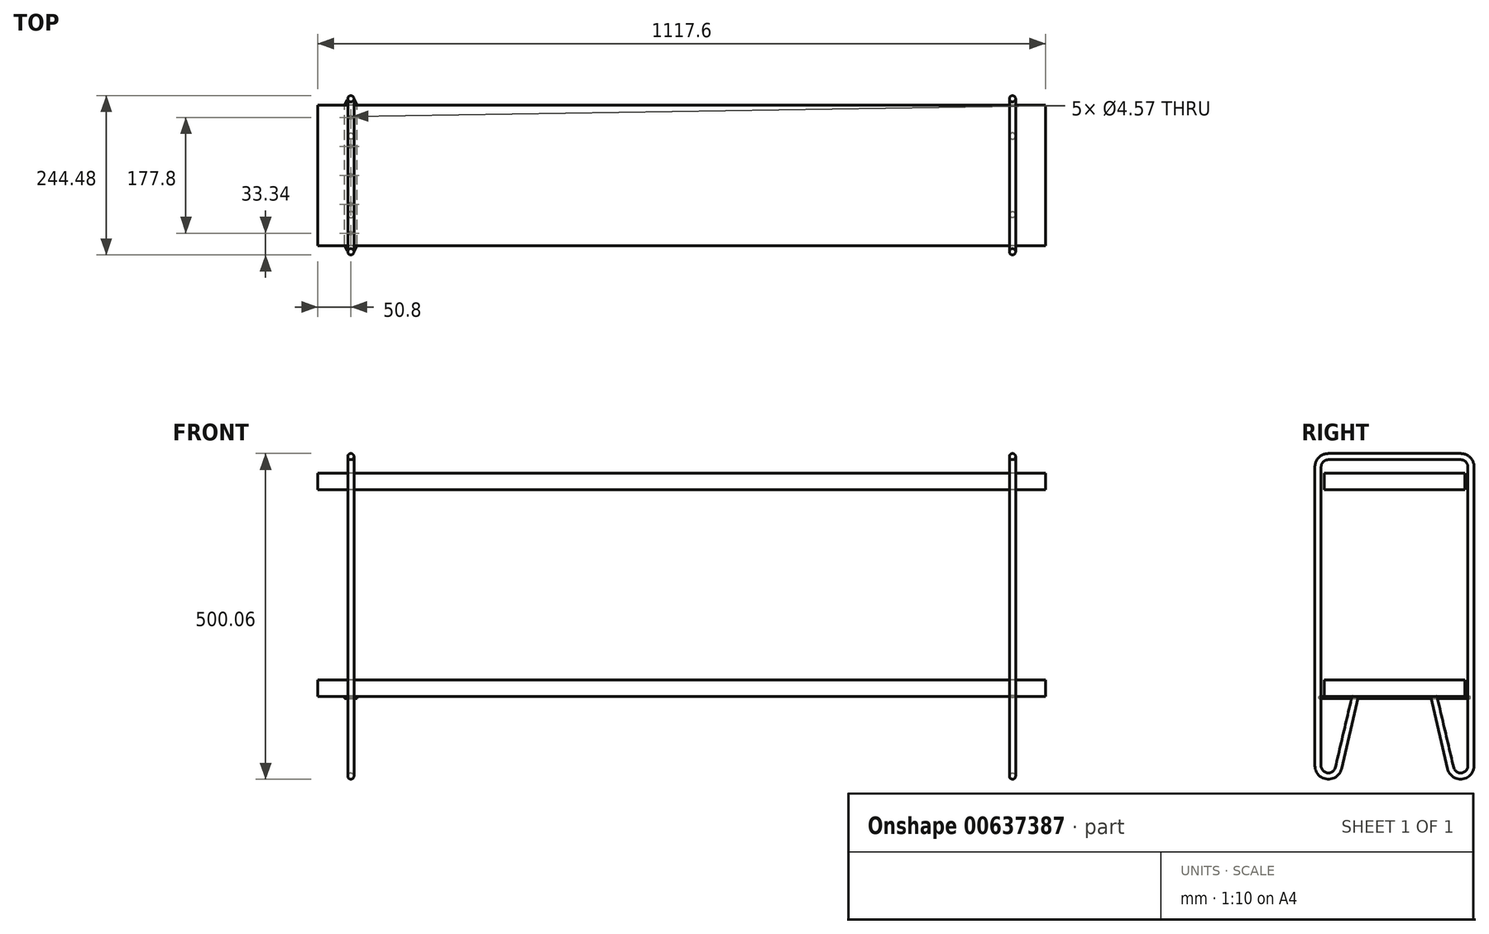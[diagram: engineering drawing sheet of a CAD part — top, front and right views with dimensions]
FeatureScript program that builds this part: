
annotation { "Feature Type Name" : "Feature", "Feature Type Description" : "" }
export const myFeature = defineFeature(function(context is Context, id is Id, definition is map)
    precondition{}
    {
        {
            var Q0;
            Q0=qCreatedBy(makeId("Right.planeOp"),FACE);
            var sketch = newSketch(context, id + "F0", { "sketchPlane" : qUnion([Q0])});
            skLineSegment(sketch, "E0", {"start": v(0, 0) * mm, "end": v(-101.6, 0) * mm});
            skLineSegment(sketch, "E1", {"start": v(-117.47, -15.88) * mm, "end": v(-117.47, -474.66) * mm});
            skLineSegment(sketch, "E2", {"start": v(-86.15, -478.3) * mm, "end": v(-60.32, -368.3) * mm});
            skLineSegment(sketch, "E3.bottom", {"start": v(-107.95, -342.9) * mm, "end": v(107.95, -342.9) * mm, "construction": true});
            skLineSegment(sketch, "E3.top", {"start": v(-107.95, -368.3) * mm, "end": v(107.95, -368.3) * mm, "construction": true});
            skLineSegment(sketch, "E3.left", {"start": v(-107.95, -342.9) * mm, "end": v(-107.95, -368.3) * mm, "construction": true});
            skLineSegment(sketch, "E3.right", {"start": v(107.95, -342.9) * mm, "end": v(107.95, -368.3) * mm, "construction": true});
            skLineSegment(sketch, "E4.bottom", {"start": v(-107.95, -25.4) * mm, "end": v(107.95, -25.4) * mm, "construction": true});
            skLineSegment(sketch, "E4.top", {"start": v(-107.95, -50.8) * mm, "end": v(107.95, -50.8) * mm, "construction": true});
            skLineSegment(sketch, "E4.left", {"start": v(-107.95, -25.4) * mm, "end": v(-107.95, -50.8) * mm, "construction": true});
            skLineSegment(sketch, "E4.right", {"start": v(107.95, -25.4) * mm, "end": v(107.95, -50.8) * mm, "construction": true});
            skLineSegment(sketch, "E5", {"start": v(-668.57, -495.3) * mm, "end": v(1361.26, -495.3) * mm, "construction": true});
            skArc(sketch, "E6", {"start": v(-117.48, -474.66) * mm, "mid": v(-103.43, -490.43) * mm, "end": v(-86.15, -478.3) * mm});
            skArc(sketch, "E7", {"start": v(-101.6, 0) * mm, "mid": v(-112.83, -4.65) * mm, "end": v(-117.47, -15.88) * mm});
            skLineSegment(sketch, "E8", {"start": v(0, -25.4) * mm, "end": v(0, 117.18) * mm, "construction": true});
            skLineSegment(sketch, "E9.MirrorCS", {"start": v(0, 0) * mm, "end": v(101.6, 0) * mm});
            skArc(sketch, "E10.MirrorCS", {"start": v(101.6, 0) * mm, "mid": v(112.83, -4.65) * mm, "end": v(117.48, -15.88) * mm});
            skLineSegment(sketch, "E11.MirrorCS", {"start": v(117.48, -15.88) * mm, "end": v(117.48, -474.66) * mm});
            skArc(sketch, "E12.MirrorCS", {"start": v(117.48, -474.66) * mm, "mid": v(103.43, -490.43) * mm, "end": v(86.15, -478.3) * mm});
            skLineSegment(sketch, "E13.MirrorCS", {"start": v(86.15, -478.3) * mm, "end": v(60.33, -368.3) * mm});
            skLineSegment(sketch, "E14.0", {"start": v(-90.78, -477.2) * mm, "end": v(-63.93, -362.81) * mm, "construction": true});
            skArc(sketch, "E14.1", {"start": v(-112.71, -474.66) * mm, "mid": v(-102.88, -485.7) * mm, "end": v(-90.78, -477.2) * mm, "construction": true});
            skLineSegment(sketch, "E14.2", {"start": v(-112.71, -15.88) * mm, "end": v(-112.71, -474.66) * mm, "construction": true});
            skArc(sketch, "E14.3", {"start": v(-101.6, -4.76) * mm, "mid": v(-109.46, -8.02) * mm, "end": v(-112.71, -15.88) * mm, "construction": true});
            skLineSegment(sketch, "E14.4", {"start": v(0, -4.76) * mm, "end": v(-101.6, -4.76) * mm, "construction": true});
            skLineSegment(sketch, "E14.5", {"start": v(0, -4.76) * mm, "end": v(101.6, -4.76) * mm, "construction": true});
            skLineSegment(sketch, "E14.6", {"start": v(90.78, -477.2) * mm, "end": v(64.62, -365.77) * mm, "construction": true});
            skArc(sketch, "E14.7", {"start": v(112.71, -474.66) * mm, "mid": v(102.88, -485.7) * mm, "end": v(90.78, -477.2) * mm, "construction": true});
            skLineSegment(sketch, "E14.8", {"start": v(112.71, -15.88) * mm, "end": v(112.71, -474.66) * mm, "construction": true});
            skArc(sketch, "E14.9", {"start": v(101.6, -4.76) * mm, "mid": v(109.46, -8.02) * mm, "end": v(112.71, -15.88) * mm, "construction": true});
            skLineSegment(sketch, "E15.0", {"start": v(-81.5, -479.38) * mm, "end": v(-55.62, -369.1) * mm, "construction": true});
            skArc(sketch, "E15.1", {"start": v(-122.24, -474.66) * mm, "mid": v(-103.97, -495.16) * mm, "end": v(-81.5, -479.38) * mm, "construction": true});
            skLineSegment(sketch, "E15.2", {"start": v(-122.24, -15.88) * mm, "end": v(-122.24, -474.66) * mm, "construction": true});
            skArc(sketch, "E15.3", {"start": v(-101.6, 4.76) * mm, "mid": v(-116.2, -1.28) * mm, "end": v(-122.24, -15.88) * mm, "construction": true});
            skLineSegment(sketch, "E15.4", {"start": v(0, 4.76) * mm, "end": v(-101.6, 4.76) * mm, "construction": true});
            skLineSegment(sketch, "E15.5", {"start": v(0, 4.76) * mm, "end": v(101.6, 4.76) * mm, "construction": true});
            skLineSegment(sketch, "E15.6", {"start": v(81.5, -479.38) * mm, "end": v(55.7, -369.44) * mm, "construction": true});
            skArc(sketch, "E15.7", {"start": v(122.24, -474.66) * mm, "mid": v(103.97, -495.16) * mm, "end": v(81.5, -479.38) * mm, "construction": true});
            skLineSegment(sketch, "E15.8", {"start": v(122.24, -15.88) * mm, "end": v(122.24, -474.66) * mm, "construction": true});
            skArc(sketch, "E15.9", {"start": v(101.6, 4.76) * mm, "mid": v(116.2, -1.28) * mm, "end": v(122.24, -15.88) * mm, "construction": true});
            skSolve(sketch);
        }
        {
            var Q0;
            Q0=qCreatedBy(makeId("Front.planeOp"),FACE);
            var sketch = newSketch(context, id + "F1", { "sketchPlane" : qUnion([Q0])});
            skCircle(sketch, "E16", {"center": v(0, 0) * mm, "radius": 4.76 * mm});
            skSolve(sketch);
        }
        {
            var Q0;
            Q0 = qSketchRegion(id + "F1", true);
            var Q1;
            Q1 = qConstructionFilter(qBodyType(qCreatedBy(id + "F0" ,EDGE), BodyType.WIRE), ConstructionObject.NO);
            sweep(context, id + "F2", {"profiles" : qUnion([Q0]), "path" : qUnion([Q1])});
        }
        {
            var Q0;
            Q0=qCreatedBy(makeId("Right.planeOp"),FACE);
            cPlane(context, id + "F3", {"entities" : qUnion([Q0]), "cplaneType" : CPlaneType.OFFSET, "offset" : 508 * mm, "width" : 152.4 * mm, "height" : 152.4 * mm});
        }
        {
            var Q0;
            Q0=makeQuery(id+"F2.opSweep","SWEPT_BODY",BODY,{"disambiguationData":[OSD([sQuery(id+"F0.wireOp",EDGE,"E13.MirrorCS"),sQuery(id+"F1.wireOp",EDGE,"E16")])]});
            var Q1;
            Q1=qCreatedBy(id+"F3.planeOp",FACE);
            mirror(context, id + "F4", {"entities" : qUnion([Q0]), "mirrorPlane" : qUnion([Q1])});
        }
        {
            var Q0;
            Q0=qCreatedBy(id+"F3.planeOp",FACE);
            var sketch = newSketch(context, id + "F5", { "sketchPlane" : qUnion([Q0])});
            skLineSegment(sketch, "E17.0", {"start": v(-107.95, -25.4) * mm, "end": v(107.95, -25.4) * mm});
            skLineSegment(sketch, "E18.0", {"start": v(-107.95, -50.8) * mm, "end": v(107.95, -50.8) * mm});
            skLineSegment(sketch, "E19.0", {"start": v(107.95, -25.4) * mm, "end": v(107.95, -50.8) * mm});
            skLineSegment(sketch, "E20.0", {"start": v(-107.95, -25.4) * mm, "end": v(-107.95, -50.8) * mm});
            skLineSegment(sketch, "E21.0", {"start": v(-107.95, -342.9) * mm, "end": v(-107.95, -368.3) * mm});
            skLineSegment(sketch, "E22.0", {"start": v(-107.95, -368.3) * mm, "end": v(107.95, -368.3) * mm});
            skLineSegment(sketch, "E23.0", {"start": v(-107.95, -342.9) * mm, "end": v(107.95, -342.9) * mm});
            skLineSegment(sketch, "E24.0", {"start": v(107.95, -342.9) * mm, "end": v(107.95, -368.3) * mm});
            skSolve(sketch);
        }
        {
            var Q0;
            Q0 = qSketchRegion(id + "F5", true);
            var Q1;
            Q1 = qConstructionFilter(qBodyType(qCreatedBy(id + "F5" ,EDGE), BodyType.WIRE), ConstructionObject.NO);
            extrude(context, id + "F6", {"entities" : qUnion([Q0]), "surfaceEntities" : qUnion([Q1]), "depth" : 558.8 * mm, "offsetDistance" : 25.4 * mm, "hasSecondDirection" : true, "secondDirectionOppositeDirection" : true, "secondDirectionDepth" : 558.8 * mm});
        }
        {
            var Q0;
            Q0=makeQuery(id+"F6.opExtrude","SWEPT_FACE",FACE,{"disambiguationData":[OSD([sQuery(id+"F5.wireOp",EDGE,"E22.0")])]});
            var sketch = newSketch(context, id + "F7", { "sketchPlane" : qUnion([Q0])});
            skArc(sketch, "E25.0", {"start": v(-4.76, 117.47) * mm, "mid": v(0, 112.71) * mm, "end": v(4.76, 117.47) * mm});
            skArc(sketch, "E26.0", {"start": v(4.76, -117.47) * mm, "mid": v(0, -112.71) * mm, "end": v(-4.76, -117.47) * mm});
            skLineSegment(sketch, "E27.left", {"start": v(-9.53, 107.95) * mm, "end": v(-9.53, -107.95) * mm});
            skLineSegment(sketch, "E27.right", {"start": v(9.52, 107.95) * mm, "end": v(9.53, -107.95) * mm});
            skLineSegment(sketch, "E28", {"start": v(-4.76, 117.47) * mm, "end": v(-9.53, 107.95) * mm});
            skLineSegment(sketch, "E29", {"start": v(4.76, 117.47) * mm, "end": v(9.52, 107.95) * mm});
            skLineSegment(sketch, "E30", {"start": v(-4.76, -117.47) * mm, "end": v(-9.53, -107.95) * mm});
            skLineSegment(sketch, "E31", {"start": v(9.53, -107.95) * mm, "end": v(4.76, -117.47) * mm});
            skPoint(sketch, "E32.orphan", {"position": v(9.53, -117.47) * mm});
            skPoint(sketch, "E33.orphan", {"position": v(-9.53, 117.47) * mm});
            skPoint(sketch, "E34.orphan", {"position": v(9.52, 117.47) * mm});
            skLineSegment(sketch, "E35", {"start": v(0, 117.47) * mm, "end": v(0, -117.47) * mm, "construction": true});
            skLineSegment(sketch, "E36", {"start": v(-9.53, 0) * mm, "end": v(9.52, 0) * mm, "construction": true});
            skCircle(sketch, "E37", {"center": v(0, 0) * mm, "radius": 2.29 * mm});
            skCircle(sketch, "E38", {"center": v(0, 44.45) * mm, "radius": 2.29 * mm});
            skCircle(sketch, "E39", {"center": v(0, 88.9) * mm, "radius": 2.29 * mm});
            skCircle(sketch, "E40.MirrorC", {"center": v(0, -44.45) * mm, "radius": 2.29 * mm});
            skCircle(sketch, "E41.MirrorC", {"center": v(0, -88.9) * mm, "radius": 2.29 * mm});
            skSolve(sketch);
        }
        {
            var Q0;
            Q0 = qSketchRegion(id + "F7", true);
            extrude(context, id + "F8", {"entities" : qUnion([Q0]), "depth" : 3.17 * mm, "offsetDistance" : 25.4 * mm});
        }
        {
            var Q0;
            Q0=makeQuery(id+"F8.opExtrude","SWEPT_EDGE",EDGE,{"disambiguationData":[OSD([sQuery(id+"F7.wireOp",EDGE,"E25.0"),sQuery(id+"F7.wireOp",EDGE,"E28")])]});
            var Q1;
            Q1=makeQuery(id+"F8.opExtrude","SWEPT_EDGE",EDGE,{"disambiguationData":[OSD([sQuery(id+"F7.wireOp",EDGE,"E25.0"),sQuery(id+"F7.wireOp",EDGE,"E29")])]});
            var Q2;
            Q2=makeQuery(id+"F8.opExtrude","SWEPT_EDGE",EDGE,{"disambiguationData":[OSD([sQuery(id+"F7.wireOp",EDGE,"E26.0"),sQuery(id+"F7.wireOp",EDGE,"E31")])]});
            var Q3;
            Q3=makeQuery(id+"F8.opExtrude","SWEPT_EDGE",EDGE,{"disambiguationData":[OSD([sQuery(id+"F7.wireOp",EDGE,"E26.0"),sQuery(id+"F7.wireOp",EDGE,"E30")])]});
            fillet(context, id + "F9", {"entities" : qUnion([Q0, Q1, Q2, Q3]), "radius" : 0.64 * mm, "tangentPropagation" : true, "allowEdgeOverflow" : false});
        }
        {
            var Q0;
            Q0=makeQuery(id+"F8.opExtrude","SWEPT_EDGE",EDGE,{"disambiguationData":[OSD([sQuery(id+"F5.wireOp",EDGE,"E22.0"),sQuery(id+"F5.wireOp",EDGE,"E24.0"),sQuery(id+"F7.wireOp",EDGE,"E27.left"),sQuery(id+"F7.wireOp",EDGE,"E30")])]});
            var Q1;
            Q1=makeQuery(id+"F8.opExtrude","SWEPT_EDGE",EDGE,{"disambiguationData":[OSD([sQuery(id+"F5.wireOp",EDGE,"E22.0"),sQuery(id+"F5.wireOp",EDGE,"E24.0"),sQuery(id+"F7.wireOp",EDGE,"E27.right"),sQuery(id+"F7.wireOp",EDGE,"E31")])]});
            var Q2;
            Q2=makeQuery(id+"F8.opExtrude","SWEPT_EDGE",EDGE,{"disambiguationData":[OSD([sQuery(id+"F5.wireOp",EDGE,"E21.0"),sQuery(id+"F5.wireOp",EDGE,"E22.0"),sQuery(id+"F7.wireOp",EDGE,"E27.right"),sQuery(id+"F7.wireOp",EDGE,"E29")])]});
            var Q3;
            Q3=makeQuery(id+"F8.opExtrude","SWEPT_EDGE",EDGE,{"disambiguationData":[OSD([sQuery(id+"F5.wireOp",EDGE,"E21.0"),sQuery(id+"F5.wireOp",EDGE,"E22.0"),sQuery(id+"F7.wireOp",EDGE,"E27.left"),sQuery(id+"F7.wireOp",EDGE,"E28")])]});
            fillet(context, id + "F10", {"entities" : qUnion([Q0, Q1, Q2, Q3]), "radius" : 6.35 * mm, "tangentPropagation" : true, "allowEdgeOverflow" : false});
        }
    });
